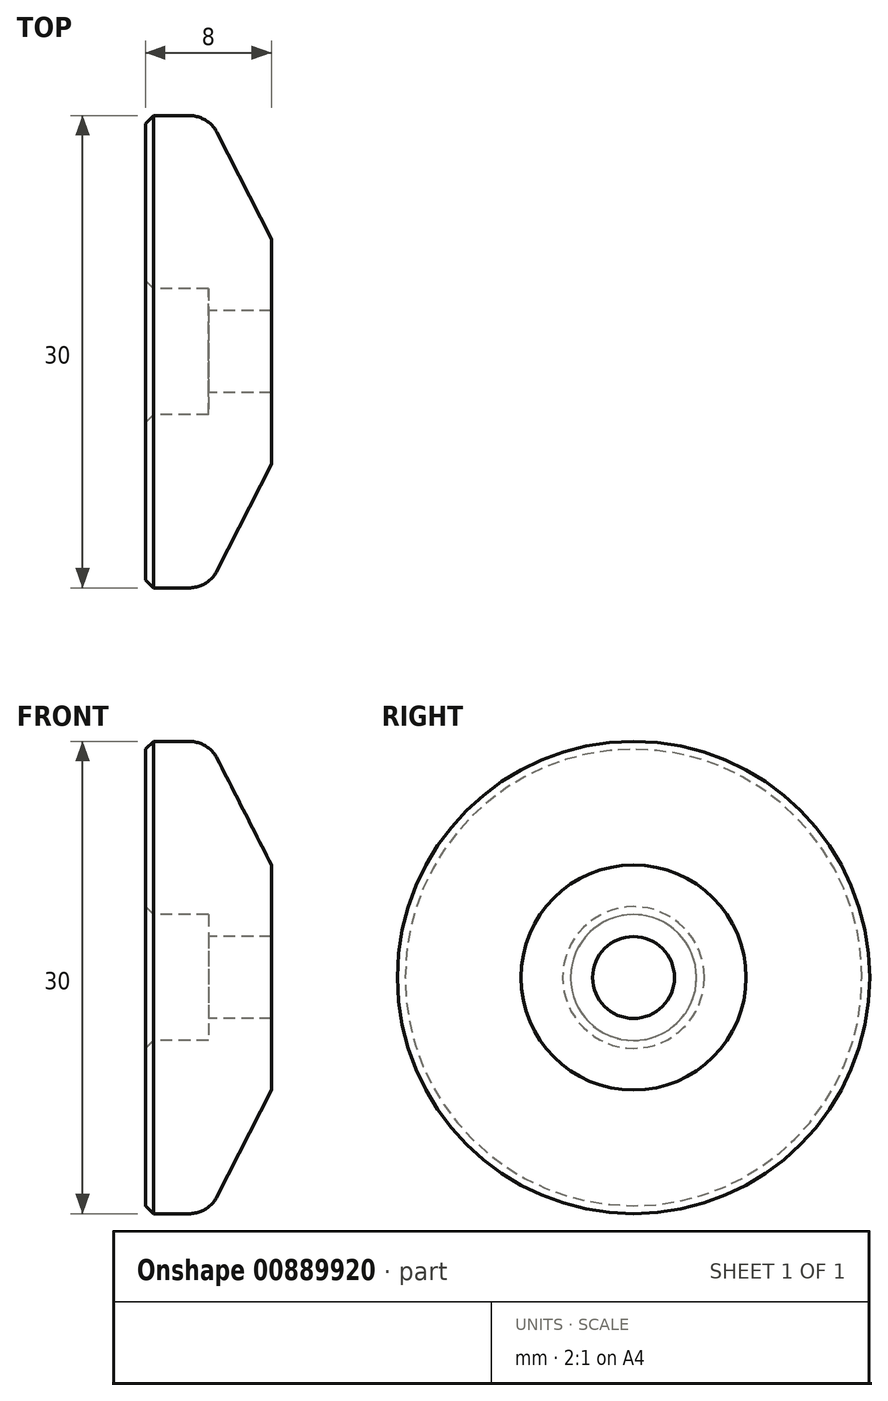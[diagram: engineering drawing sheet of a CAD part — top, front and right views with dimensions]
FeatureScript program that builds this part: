
annotation { "Feature Type Name" : "Feature", "Feature Type Description" : "" }
export const myFeature = defineFeature(function(context is Context, id is Id, definition is map)
    precondition{}
    {
        {
            var Q0;
            Q0=qCreatedBy(makeId("Front.planeOp"),FACE);
            var sketch = newSketch(context, id + "F0", { "sketchPlane" : qUnion([Q0])});
            skLineSegment(sketch, "E0", {"start": v(0, 15) * mm, "end": v(0, 4) * mm});
            skLineSegment(sketch, "E1", {"start": v(0, 4) * mm, "end": v(4, 4) * mm});
            skLineSegment(sketch, "E2", {"start": v(4, 4) * mm, "end": v(4, 2.6) * mm});
            skLineSegment(sketch, "E3", {"start": v(4, 2.6) * mm, "end": v(8, 2.6) * mm});
            skLineSegment(sketch, "E4", {"start": v(8, 2.6) * mm, "end": v(8, 7.15) * mm});
            skLineSegment(sketch, "E5", {"start": v(8, 7.15) * mm, "end": v(4, 15) * mm});
            skLineSegment(sketch, "E6", {"start": v(4, 15) * mm, "end": v(0, 15) * mm});
            skLineSegment(sketch, "E7", {"start": v(0, 0) * mm, "end": v(25.6, 0) * mm, "construction": true});
            skSolve(sketch);
        }
        {
            var Q0;
            Q0 = qSketchRegion(id + "F0", true);
            var Q1;
            Q1=sQuery(id+"F0.wireOp",EDGE,"E7");
            revolve(context, id + "F1", {"surfaceOperationType" : NewSurfaceOperationType.NEW, "entities" : qUnion([Q0]), "axis" : qUnion([Q1]), "revolveType" : RevolveType.FULL});
        }
        {
            var Q0;
            Q0=makeQuery(id+"F1.opRevolve","SWEPT_EDGE",EDGE,{"disambiguationData":[OSD([sQuery(id+"F0.wireOp",EDGE,"E5"),sQuery(id+"F0.wireOp",EDGE,"E6")])]});
            fillet(context, id + "F2", {"entities" : qUnion([Q0]), "radius" : 2 * mm, "tangentPropagation" : true, "allowEdgeOverflow" : false});
        }
        {
            var Q0;
            Q0=makeQuery(id+"F1.opRevolve","SWEPT_EDGE",EDGE,{"disambiguationData":[OSD([sQuery(id+"F0.wireOp",EDGE,"E0"),sQuery(id+"F0.wireOp",EDGE,"E1")])]});
            var Q1;
            Q1=makeQuery(id+"F1.opRevolve","SWEPT_EDGE",EDGE,{"disambiguationData":[OSD([sQuery(id+"F0.wireOp",EDGE,"E0"),sQuery(id+"F0.wireOp",EDGE,"E6")])]});
            chamfer(context, id + "F3", {"entities" : qUnion([Q0, Q1]), "width" : 0.5 * mm, "tangentPropagation" : true});
        }
    });
